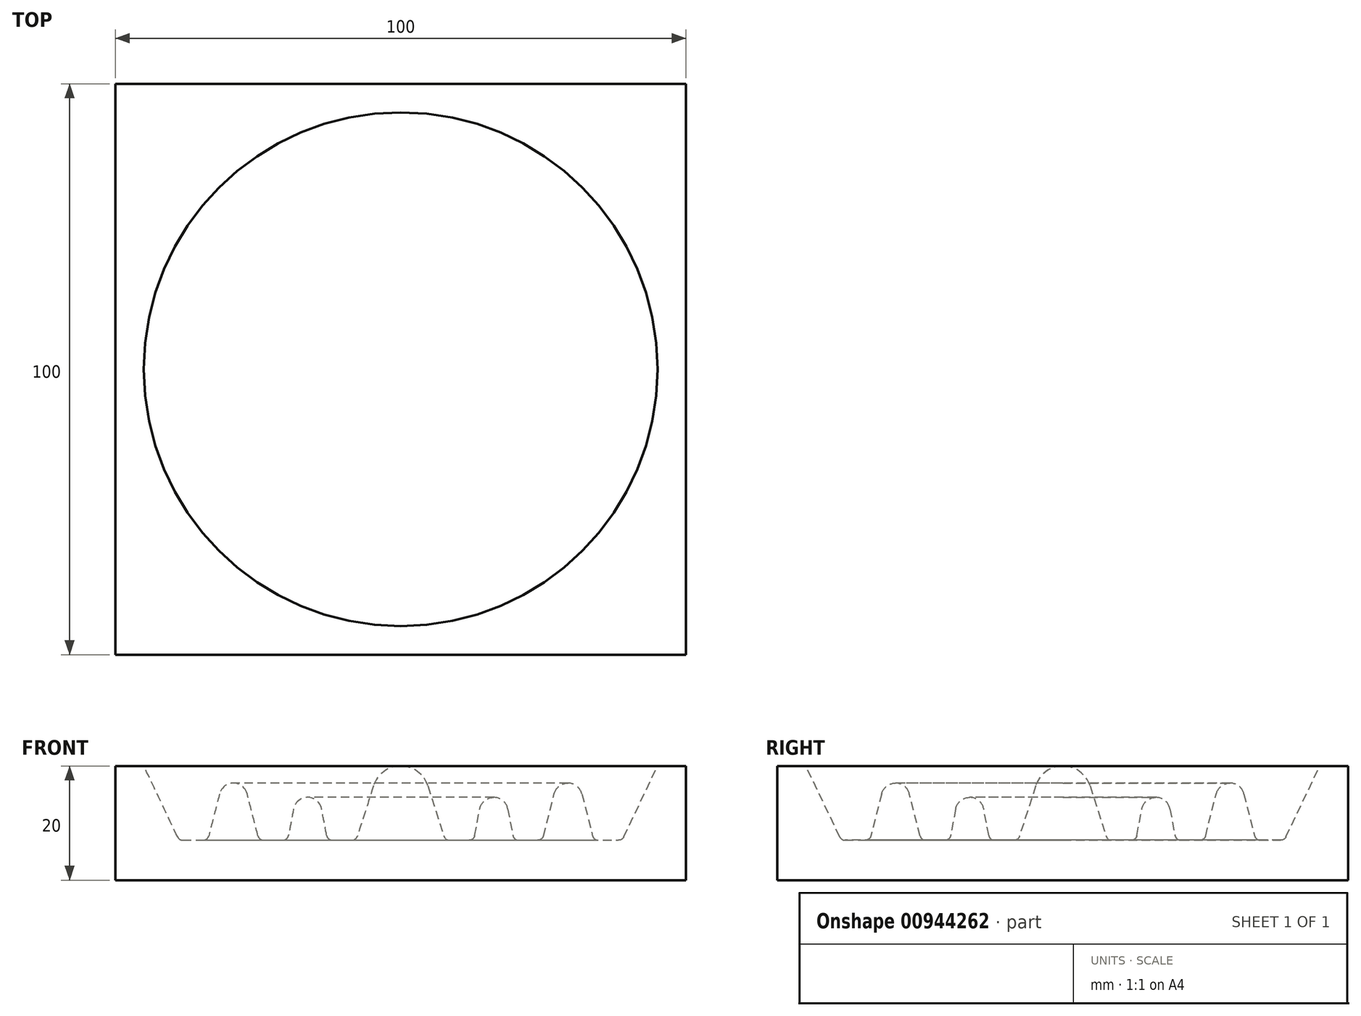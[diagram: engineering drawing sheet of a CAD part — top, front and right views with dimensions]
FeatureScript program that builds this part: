
annotation { "Feature Type Name" : "Feature", "Feature Type Description" : "" }
export const myFeature = defineFeature(function(context is Context, id is Id, definition is map)
    precondition{}
    {
        {
            var Q0;
            Q0=qCreatedBy(makeId("Top.planeOp"),FACE);
            var sketch = newSketch(context, id + "F0", { "sketchPlane" : qUnion([Q0])});
            skLineSegment(sketch, "E0.bottom", {"start": v(0, 0) * mm, "end": v(100, 0) * mm});
            skLineSegment(sketch, "E0.top", {"start": v(0, 100) * mm, "end": v(100, 100) * mm});
            skLineSegment(sketch, "E0.left", {"start": v(0, 0) * mm, "end": v(0, 100) * mm});
            skLineSegment(sketch, "E0.right", {"start": v(100, 0) * mm, "end": v(100, 100) * mm});
            skSolve(sketch);
        }
        {
            var Q0;
            Q0 = qSketchRegion(id + "F0", true);
            extrude(context, id + "F1", {"entities" : qUnion([Q0]), "depth" : 20 * mm, "offsetDistance" : 25 * mm});
        }
        {
            var Q0;
            Q0=makeQuery(id+"F1.opExtrude","SWEPT_FACE",FACE,{"disambiguationData":[OSD([sQuery(id+"F0.wireOp",EDGE,"E0.right")])]});
            cPlane(context, id + "F2", {"entities" : qUnion([Q0]), "cplaneType" : CPlaneType.OFFSET, "offset" : 50 * mm, "oppositeDirection" : true, "width" : 150 * mm, "height" : 150 * mm});
        }
        {
            var Q0;
            Q0=qCreatedBy(id+"F2.planeOp",FACE);
            var sketch = newSketch(context, id + "F3", { "sketchPlane" : qUnion([Q0])});
            skArc(sketch, "E1", {"start": v(50, 20) * mm, "mid": v(47.05, 19.04) * mm, "end": v(45.24, 16.52) * mm});
            skLineSegment(sketch, "E2", {"start": v(50, 40.87) * mm, "end": v(50, -6.75) * mm, "construction": true});
            skLineSegment(sketch, "E3", {"start": v(45.24, 16.52) * mm, "end": v(42.41, 7.7) * mm});
            skLineSegment(sketch, "E4", {"start": v(10.92, 7.57) * mm, "end": v(5, 20) * mm});
            skArc(sketch, "E5", {"start": v(36.15, 12.47) * mm, "mid": v(33.69, 14.5) * mm, "end": v(31.23, 12.47) * mm});
            skArc(sketch, "E6", {"start": v(23.11, 15.12) * mm, "mid": v(20.69, 17) * mm, "end": v(18.27, 15.12) * mm});
            skLineSegment(sketch, "E7", {"start": v(50, 20) * mm, "end": v(50, 25.97) * mm});
            skLineSegment(sketch, "E8", {"start": v(50, 25.97) * mm, "end": v(5, 25.97) * mm});
            skLineSegment(sketch, "E9", {"start": v(5, 25.97) * mm, "end": v(5, 20) * mm});
            skLineSegment(sketch, "E10", {"start": v(18.27, 15.12) * mm, "end": v(16.38, 7.75) * mm});
            skLineSegment(sketch, "E11", {"start": v(23.11, 15.12) * mm, "end": v(25, 7.75) * mm});
            skLineSegment(sketch, "E12", {"start": v(31.23, 12.47) * mm, "end": v(30.34, 7.81) * mm});
            skLineSegment(sketch, "E13", {"start": v(36.15, 12.47) * mm, "end": v(37.03, 7.81) * mm});
            skLineSegment(sketch, "E14", {"start": v(15.41, 7) * mm, "end": v(11.82, 7) * mm});
            skLineSegment(sketch, "E15", {"start": v(25.97, 7) * mm, "end": v(29.36, 7) * mm});
            skLineSegment(sketch, "E16", {"start": v(38.02, 7) * mm, "end": v(41.46, 7) * mm});
            skPoint(sketch, "E17.visualSharp", {"position": v(16.19, 7) * mm});
            skArc(sketch, "E17.filletArc", {"start": v(15.41, 7) * mm, "mid": v(16.03, 7.21) * mm, "end": v(16.38, 7.75) * mm});
            skPoint(sketch, "E18.visualSharp", {"position": v(25.19, 7) * mm});
            skArc(sketch, "E18.filletArc", {"start": v(25, 7.75) * mm, "mid": v(25.35, 7.21) * mm, "end": v(25.97, 7) * mm});
            skPoint(sketch, "E19.visualSharp", {"position": v(30.19, 7) * mm});
            skArc(sketch, "E19.filletArc", {"start": v(29.36, 7) * mm, "mid": v(30, 7.23) * mm, "end": v(30.34, 7.81) * mm});
            skPoint(sketch, "E20.visualSharp", {"position": v(37.19, 7) * mm});
            skArc(sketch, "E20.filletArc", {"start": v(37.03, 7.81) * mm, "mid": v(37.38, 7.23) * mm, "end": v(38.02, 7) * mm});
            skPoint(sketch, "E21.visualSharp", {"position": v(42.19, 7) * mm});
            skArc(sketch, "E21.filletArc", {"start": v(41.46, 7) * mm, "mid": v(42.05, 7.2) * mm, "end": v(42.41, 7.7) * mm});
            skPoint(sketch, "E22.visualSharp", {"position": v(11.19, 7) * mm});
            skArc(sketch, "E22.filletArc", {"start": v(10.92, 7.57) * mm, "mid": v(11.29, 7.15) * mm, "end": v(11.82, 7) * mm});
            skSolve(sketch);
        }
        {
            var Q0;
            Q0=makeQuery(id+"F3.imprint","IMPRINT",FACE,{"disambiguationData":[TD([[makeQuery(id+"F3.imprint","IMPRINT",EDGE,{"derivedFrom":sQuery(id+"F3.wireOp",EDGE,"E1")}),-1.0]])]});
            var Q1;
            Q1=sQuery(id+"F3.wireOp",EDGE,"E2");
            revolve(context, id + "F4", {"operationType" : NewBodyOperationType.REMOVE, "surfaceOperationType" : NewSurfaceOperationType.NEW, "entities" : qUnion([Q0]), "axis" : qUnion([Q1]), "revolveType" : RevolveType.FULL, "oppositeDirection" : true});
        }
    });
